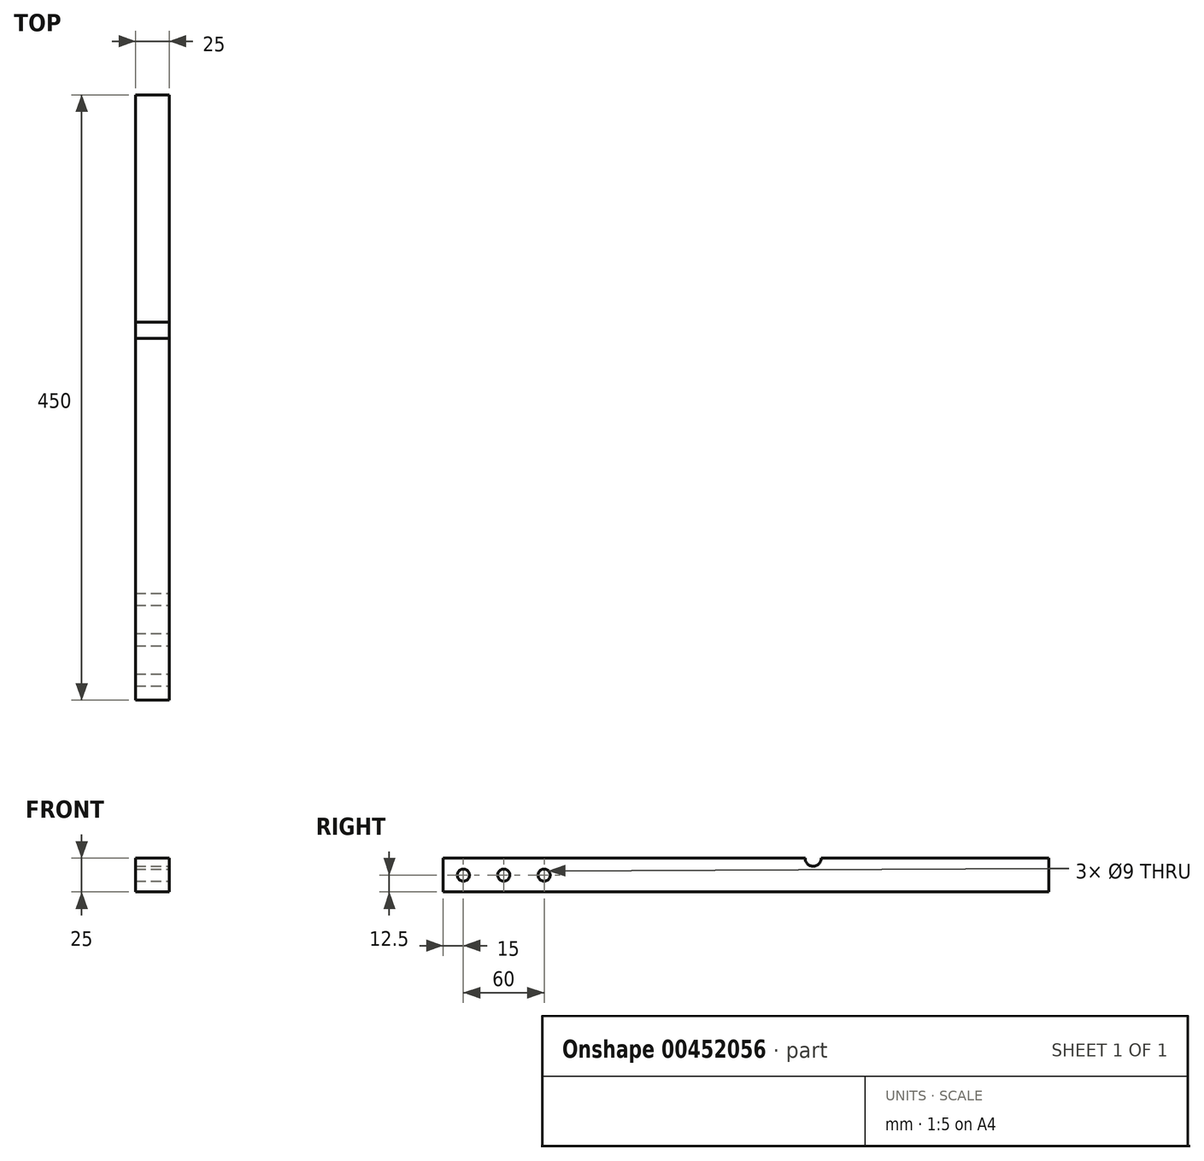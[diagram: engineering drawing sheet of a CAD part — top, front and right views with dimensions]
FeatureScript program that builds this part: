
annotation { "Feature Type Name" : "Feature", "Feature Type Description" : "" }
export const myFeature = defineFeature(function(context is Context, id is Id, definition is map)
    precondition{}
    {
        {
            var Q0;
            Q0=qCreatedBy(makeId("Right.planeOp"),FACE);
            var sketch = newSketch(context, id + "F0", { "sketchPlane" : qUnion([Q0])});
            skLineSegment(sketch, "E0.bottom", {"start": v(0, 25) * mm, "end": v(350, 25) * mm});
            skLineSegment(sketch, "E0.top", {"start": v(0, 0) * mm, "end": v(350, 0) * mm});
            skLineSegment(sketch, "E0.left", {"start": v(0, 25) * mm, "end": v(0, 0) * mm});
            skLineSegment(sketch, "E0.right", {"start": v(350, 25) * mm, "end": v(350, 0) * mm});
            skSolve(sketch);
        }
        {
            var Q0;
            Q0 = qSketchRegion(id + "F0", true);
            extrude(context, id + "F1", {"entities" : qUnion([Q0]), "depth" : 12.5 * mm, "hasSecondDirection" : true, "secondDirectionOppositeDirection" : true, "secondDirectionDepth" : 12.5 * mm});
        }
        {
            var Q0;
            Q0=makeQuery(id+"F1.opExtrude","CAP_FACE",FACE,{"disambiguationData":[OSD([sQuery(id+"F0.wireOp",EDGE,"E0.bottom"),sQuery(id+"F0.wireOp",EDGE,"E0.top"),sQuery(id+"F0.wireOp",EDGE,"E0.left"),sQuery(id+"F0.wireOp",EDGE,"E0.right")])],"isStart":false});
            var sketch = newSketch(context, id + "F2", { "sketchPlane" : qUnion([Q0])});
            skCircle(sketch, "E1", {"center": v(175, 25) * mm, "radius": 6 * mm});
            skSolve(sketch);
        }
        {
            var Q0;
            {var subQ0=sQuery(id+"F2.wireOp",EDGE,"E1");var subQ1=makeQuery(id+"F1.opExtrude","CAP_EDGE",EDGE,{"disambiguationData":[OSD([sQuery(id+"F0.wireOp",EDGE,"E0.bottom")])],"isStart":false});var subQ2=makeQuery(id+"F2.imprint","INTERSECT",VERTEX,{"disambiguationData":[OD(0.0)],"derivedFrom":[subQ1,subQ0]});Q0=makeQuery(id+"F2.imprint","IMPRINT",FACE,{"disambiguationData":[TD([[makeQuery(id+"F2.imprint","IMPRINT",EDGE,{"disambiguationData":[TD([[subQ2,-1.0]])],"derivedFrom":subQ0}),1.0]])]});}
            extrude(context, id + "F3", {"entities" : qUnion([Q0]), "operationType" : NewBodyOperationType.REMOVE, "oppositeDirection" : true, "depth" : 25 * mm});
        }
        {
            var Q0;
            {var subQ1=sQuery(id+"F0.wireOp",EDGE,"E0.left");var subQ3=sQuery(id+"F0.wireOp",EDGE,"E0.bottom");Q0=makeQuery(id+"F3.boolean.opBoolean","SPLIT",FACE,{"disambiguationData":[TD([makeQuery(id+"F1.opExtrude","SWEPT_FACE",FACE,{"disambiguationData":[OSD([subQ1])]})])],"derivedFrom":makeQuery(id+"F1.opExtrude","SWEPT_FACE",FACE,{"disambiguationData":[OSD([subQ3])]})});}
            var Q1;
            Q1=makeQuery(id+"F1.opExtrude","SWEPT_FACE",FACE,{"disambiguationData":[OSD([sQuery(id+"F0.wireOp",EDGE,"E0.top")])]});
            cPlane(context, id + "F4", {"entities" : qUnion([Q0, Q1]), "cplaneType" : CPlaneType.MID_PLANE, "offset" : 25 * mm, "width" : 150 * mm, "height" : 150 * mm});
        }
        {
            var Q0;
            Q0=makeQuery(id+"F1.opExtrude","SWEPT_FACE",FACE,{"disambiguationData":[OSD([sQuery(id+"F0.wireOp",EDGE,"E0.left")])]});
            extrude(context, id + "F5", {"entities" : qUnion([Q0]), "operationType" : NewBodyOperationType.ADD, "depth" : 100 * mm});
        }
        {
            var Q0;
            {var subQ0=sQuery(id+"F0.wireOp",EDGE,"E0.left");Q0=makeQuery(id+"F5.boolean.opBoolean","MERGE",FACE,{"derivedFrom":[makeQuery(id+"F1.opExtrude","CAP_FACE",FACE,{"disambiguationData":[OSD([sQuery(id+"F0.wireOp",EDGE,"E0.bottom"),sQuery(id+"F0.wireOp",EDGE,"E0.top"),subQ0,sQuery(id+"F0.wireOp",EDGE,"E0.right")])],"isStart":false}),makeQuery(id+"F5.opExtrude","SWEPT_FACE",FACE,{"disambiguationData":[OSD([subQ0]),TDD([makeQuery(id+"F1.opExtrude","CAP_EDGE",EDGE,{"disambiguationData":[OSD([subQ0])],"isStart":false})])]})]});}
            var sketch = newSketch(context, id + "F6", { "sketchPlane" : qUnion([Q0])});
            skLineSegment(sketch, "E2", {"start": v(-100, 12.5) * mm, "end": v(0, 12.5) * mm, "construction": true});
            skPoint(sketch, "E3", {"position": v(-85, 12.5) * mm});
            skPoint(sketch, "E4", {"position": v(-55, 12.5) * mm});
            skPoint(sketch, "E5", {"position": v(-25, 12.5) * mm});
            skSolve(sketch);
        }
        {
            var Q0;
            Q0=sQuery(id+"F6.wireOp",VERTEX,"E3");
            var Q1;
            Q1=sQuery(id+"F6.wireOp",VERTEX,"E4");
            var Q2;
            Q2=sQuery(id+"F6.wireOp",VERTEX,"E5");
            var Q3;
            Q3=makeQuery(id+"F1.opExtrude","SWEPT_BODY",BODY,{"disambiguationData":[OSD([sQuery(id+"F0.wireOp",EDGE,"E0.bottom"),sQuery(id+"F0.wireOp",EDGE,"E0.top"),sQuery(id+"F0.wireOp",EDGE,"E0.left"),sQuery(id+"F0.wireOp",EDGE,"E0.right")])]});
            hole(context, id + "F7", {"style" : HoleStyle.SIMPLE, "endStyle" : HoleEndStyle.THROUGH, "standardTappedOrClearance" : lookupTablePath({ "standard" : "ISO", "size" : "9", "type" : "Drilled" }), "standardBlindInLast" : lookupTablePath({ "standard" : "ISO", "size" : "9", "type" : "Drilled" }), "holeDiameter" : 9 * mm, "isTappedThrough" : true, "tappedDepth" : 12 * mm, "tapClearance" : 3, "locations" : qUnion([Q0, Q1, Q2]), "scope" : qUnion([Q3])});
        }
    });
